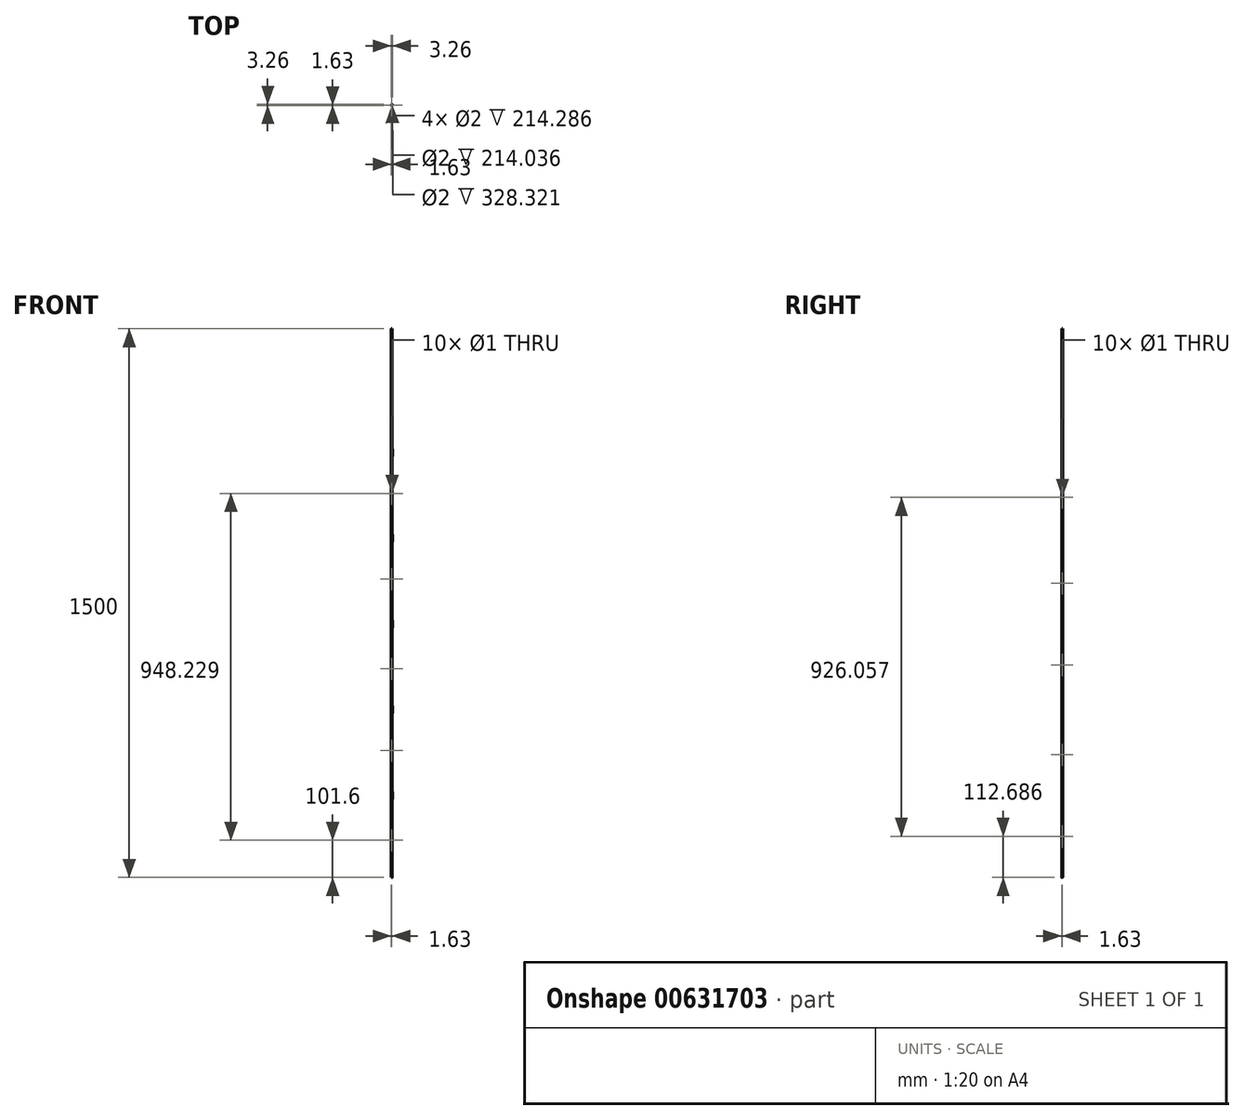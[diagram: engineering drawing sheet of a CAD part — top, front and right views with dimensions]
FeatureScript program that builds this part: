
annotation { "Feature Type Name" : "Feature", "Feature Type Description" : "" }
export const myFeature = defineFeature(function(context is Context, id is Id, definition is map)
    precondition{}
    {
        {
            var Q0;
            Q0=qCreatedBy(makeId("Top.planeOp"),FACE);
            var sketch = newSketch(context, id + "F0", { "sketchPlane" : qUnion([Q0])});
            skCircle(sketch, "E0", {"center": v(0, 0) * mm, "radius": 1 * mm});
            skCircle(sketch, "E1", {"center": v(0, 0) * mm, "radius": 1.25 * mm});
            skSolve(sketch);
        }
        {
            var Q0;
            Q0=makeQuery(id+"F0.imprint","IMPRINT",FACE,{"disambiguationData":[TD([[makeQuery(id+"F0.imprint","IMPRINT",EDGE,{"derivedFrom":sQuery(id+"F0.wireOp",EDGE,"E0")}),-1.0]])]});
            extrude(context, id + "F1", {"entities" : qUnion([Q0]), "depth" : 1500 * mm, "offsetDistance" : 25.4 * mm});
        }
        {
            var Q0;
            Q0=qCreatedBy(makeId("Front.planeOp"),FACE);
            var sketch = newSketch(context, id + "F2", { "sketchPlane" : qUnion([Q0])});
            skLineSegment(sketch, "E2.bottom", {"start": v(0, 214.29) * mm, "end": v(1.62, 214.29) * mm});
            skLineSegment(sketch, "E2.top", {"start": v(0, 234.29) * mm, "end": v(1.62, 234.29) * mm});
            skLineSegment(sketch, "E2.left", {"start": v(0, 214.29) * mm, "end": v(0, 234.29) * mm});
            skLineSegment(sketch, "E2.right", {"start": v(1.63, 214.29) * mm, "end": v(1.63, 234.29) * mm});
            skLineSegment(sketch, "E3", {"start": v(0, -76.39) * mm, "end": v(0, 107.51) * mm});
            skLineSegment(sketch, "E4.bottom", {"start": v(0, 448.57) * mm, "end": v(1.62, 448.57) * mm});
            skLineSegment(sketch, "E4.top", {"start": v(0, 468.57) * mm, "end": v(1.62, 468.57) * mm});
            skLineSegment(sketch, "E4.left", {"start": v(0, 448.57) * mm, "end": v(0, 468.57) * mm});
            skLineSegment(sketch, "E4.right", {"start": v(1.62, 448.57) * mm, "end": v(1.62, 468.57) * mm});
            skLineSegment(sketch, "E5.bottom", {"start": v(0, 682.86) * mm, "end": v(1.62, 682.86) * mm});
            skLineSegment(sketch, "E5.top", {"start": v(0, 702.86) * mm, "end": v(1.62, 702.86) * mm});
            skLineSegment(sketch, "E5.left", {"start": v(0, 682.86) * mm, "end": v(0, 702.86) * mm});
            skLineSegment(sketch, "E5.right", {"start": v(1.62, 682.86) * mm, "end": v(1.62, 702.86) * mm});
            skLineSegment(sketch, "E6.bottom", {"start": v(0, 937.14) * mm, "end": v(1.63, 937.14) * mm});
            skLineSegment(sketch, "E6.top", {"start": v(0, 917.14) * mm, "end": v(1.63, 917.14) * mm});
            skLineSegment(sketch, "E6.left", {"start": v(0, 937.14) * mm, "end": v(0, 917.14) * mm});
            skLineSegment(sketch, "E6.right", {"start": v(1.62, 937.14) * mm, "end": v(1.62, 917.14) * mm});
            skLineSegment(sketch, "E7.bottom", {"start": v(0, 1151.43) * mm, "end": v(1.62, 1151.43) * mm});
            skLineSegment(sketch, "E7.top", {"start": v(0, 1171.43) * mm, "end": v(1.62, 1171.43) * mm});
            skLineSegment(sketch, "E7.left", {"start": v(0, 1151.43) * mm, "end": v(0, 1171.43) * mm});
            skLineSegment(sketch, "E7.right", {"start": v(1.62, 1151.43) * mm, "end": v(1.62, 1171.43) * mm});
            skSolve(sketch);
        }
        {
            var Q0;
            {var subQ0=sQuery(id+"F2.wireOp",EDGE,"E2.bottom");Q0=makeQuery(id+"F2.imprint","IMPRINT",FACE,{"disambiguationData":[TD([[makeQuery(id+"F2.imprint","IMPRINT",EDGE,{"derivedFrom":subQ0}),1.0]])]});}
            var Q1;
            Q1=sQuery(id+"F2.wireOp",EDGE,"E3");
            revolve(context, id + "F3", {"operationType" : NewBodyOperationType.ADD, "entities" : qUnion([Q0]), "axis" : qUnion([Q1]), "revolveType" : RevolveType.FULL});
        }
        {
            var Q0;
            Q0=qCreatedBy(makeId("Front.planeOp"),FACE);
            var sketch = newSketch(context, id + "F4", { "sketchPlane" : qUnion([Q0])});
            skLineSegment(sketch, "E8", {"start": v(0, -76.07) * mm, "end": v(0, 1560.8) * mm});
            skSolve(sketch);
        }
        {
            var Q0;
            Q0=makeQuery(id+"F2.imprint","IMPRINT",FACE,{"disambiguationData":[TD([[makeQuery(id+"F2.imprint","IMPRINT",EDGE,{"derivedFrom":sQuery(id+"F2.wireOp",EDGE,"E4.bottom")}),1.0]])]});
            var Q1;
            Q1=sQuery(id+"F4.wireOp",EDGE,"E8");
            revolve(context, id + "F5", {"operationType" : NewBodyOperationType.ADD, "entities" : qUnion([Q0]), "axis" : qUnion([Q1]), "revolveType" : RevolveType.FULL});
        }
        {
            var Q0;
            Q0=makeQuery(id+"F2.imprint","IMPRINT",FACE,{"disambiguationData":[TD([[makeQuery(id+"F2.imprint","IMPRINT",EDGE,{"derivedFrom":sQuery(id+"F2.wireOp",EDGE,"E5.bottom")}),1.0]])]});
            var Q1;
            Q1=sQuery(id+"F4.wireOp",EDGE,"E8");
            revolve(context, id + "F6", {"operationType" : NewBodyOperationType.ADD, "entities" : qUnion([Q0]), "axis" : qUnion([Q1]), "revolveType" : RevolveType.FULL});
        }
        {
            var Q0;
            Q0=makeQuery(id+"F2.imprint","IMPRINT",FACE,{"disambiguationData":[TD([[makeQuery(id+"F2.imprint","IMPRINT",EDGE,{"derivedFrom":sQuery(id+"F2.wireOp",EDGE,"E6.bottom")}),-1.0]])]});
            var Q1;
            Q1=sQuery(id+"F4.wireOp",EDGE,"E8");
            revolve(context, id + "F7", {"entities" : qUnion([Q0]), "axis" : qUnion([Q1]), "revolveType" : RevolveType.FULL});
        }
        {
            var Q0;
            Q0=makeQuery(id+"F2.imprint","IMPRINT",FACE,{"disambiguationData":[TD([[makeQuery(id+"F2.imprint","IMPRINT",EDGE,{"derivedFrom":sQuery(id+"F2.wireOp",EDGE,"E6.bottom")}),-1.0]])]});
            var Q1;
            Q1=sQuery(id+"F4.wireOp",EDGE,"E8");
            revolve(context, id + "F8", {"operationType" : NewBodyOperationType.ADD, "entities" : qUnion([Q0]), "axis" : qUnion([Q1]), "revolveType" : RevolveType.FULL});
        }
        {
            var Q0;
            Q0=makeQuery(id+"F2.imprint","IMPRINT",FACE,{"disambiguationData":[TD([[makeQuery(id+"F2.imprint","IMPRINT",EDGE,{"derivedFrom":sQuery(id+"F2.wireOp",EDGE,"E7.bottom")}),1.0]])]});
            var Q1;
            Q1=sQuery(id+"F4.wireOp",EDGE,"E8");
            revolve(context, id + "F9", {"operationType" : NewBodyOperationType.ADD, "entities" : qUnion([Q0]), "axis" : qUnion([Q1]), "revolveType" : RevolveType.FULL});
        }
        {
            var Q0;
            Q0=qCreatedBy(makeId("Front.planeOp"),FACE);
            var sketch = newSketch(context, id + "F10", { "sketchPlane" : qUnion([Q0])});
            skCircle(sketch, "E9", {"center": v(0, 101.6) * mm, "radius": 0.5 * mm});
            skLineSegment(sketch, "E10", {"start": v(0, 224.29) * mm, "end": v(19.28, 224.29) * mm});
            skCircle(sketch, "E11.MirrorC", {"center": v(0, 346.97) * mm, "radius": 0.5 * mm});
            skSolve(sketch);
        }
        {
            var Q0;
            Q0 = qSketchRegion(id + "F10", true);
            extrude(context, id + "F11", {"entities" : qUnion([Q0]), "operationType" : NewBodyOperationType.REMOVE, "endBound" : BoundingType.SYMMETRIC, "oppositeDirection" : true, "depth" : 25.4 * mm, "offsetDistance" : 25.4 * mm});
        }
        {
            var Q0;
            Q0=qCreatedBy(makeId("Right.planeOp"),FACE);
            var sketch = newSketch(context, id + "F12", { "sketchPlane" : qUnion([Q0])});
            skCircle(sketch, "E12", {"center": v(0, 112.69) * mm, "radius": 0.5 * mm});
            skLineSegment(sketch, "E13", {"start": v(0, 224.29) * mm, "end": v(-15.1, 224.29) * mm});
            skCircle(sketch, "E14.MirrorC", {"center": v(0, 335.89) * mm, "radius": 0.5 * mm});
            skSolve(sketch);
        }
        {
            var Q0;
            Q0 = qSketchRegion(id + "F12", true);
            extrude(context, id + "F13", {"entities" : qUnion([Q0]), "operationType" : NewBodyOperationType.REMOVE, "endBound" : BoundingType.SYMMETRIC, "depth" : 25.4 * mm, "offsetDistance" : 25.4 * mm});
        }
        {
            var Q0;
            Q0=qCreatedBy(makeId("Front.planeOp"),FACE);
            var sketch = newSketch(context, id + "F14", { "sketchPlane" : qUnion([Q0])});
            skLineSegment(sketch, "E15", {"start": v(0, 692.86) * mm, "end": v(-20.67, 692.86) * mm});
            skSolve(sketch);
        }
        {
            var Q0;
            Q0=qCreatedBy(makeId("Front.planeOp"),FACE);
            var sketch = newSketch(context, id + "F15", { "sketchPlane" : qUnion([Q0])});
            skCircle(sketch, "E16", {"center": v(0, 570.17) * mm, "radius": 0.5 * mm});
            skCircle(sketch, "E17.MirrorC", {"center": v(0, 815.54) * mm, "radius": 0.5 * mm});
            skSolve(sketch);
        }
        {
            var Q0;
            Q0 = qSketchRegion(id + "F15", true);
            extrude(context, id + "F16", {"entities" : qUnion([Q0]), "operationType" : NewBodyOperationType.REMOVE, "endBound" : BoundingType.SYMMETRIC, "oppositeDirection" : true, "depth" : 25.4 * mm, "offsetDistance" : 25.4 * mm});
        }
        {
            var Q0;
            Q0=qCreatedBy(makeId("Right.planeOp"),FACE);
            var sketch = newSketch(context, id + "F17", { "sketchPlane" : qUnion([Q0])});
            skCircle(sketch, "E18", {"center": v(0, 804.46) * mm, "radius": 0.5 * mm});
            skSolve(sketch);
        }
        {
            var Q0;
            Q0 = qSketchRegion(id + "F17", true);
            extrude(context, id + "F18", {"entities" : qUnion([Q0]), "operationType" : NewBodyOperationType.REMOVE, "endBound" : BoundingType.SYMMETRIC, "depth" : 25.4 * mm, "offsetDistance" : 25.4 * mm});
        }
        {
            var Q0;
            Q0=qCreatedBy(makeId("Right.planeOp"),FACE);
            var sketch = newSketch(context, id + "F19", { "sketchPlane" : qUnion([Q0])});
            skCircle(sketch, "E19", {"center": v(0, 581.26) * mm, "radius": 0.5 * mm});
            skSolve(sketch);
        }
        {
            var Q0;
            Q0 = qSketchRegion(id + "F19", true);
            extrude(context, id + "F20", {"entities" : qUnion([Q0]), "operationType" : NewBodyOperationType.REMOVE, "endBound" : BoundingType.SYMMETRIC, "depth" : 25.4 * mm, "offsetDistance" : 25.4 * mm});
        }
        {
            var Q0;
            Q0=qCreatedBy(makeId("Right.planeOp"),FACE);
            var sketch = newSketch(context, id + "F21", { "sketchPlane" : qUnion([Q0])});
            skCircle(sketch, "E20", {"center": v(0, 1038.74) * mm, "radius": 0.5 * mm});
            skSolve(sketch);
        }
        {
            var Q0;
            Q0 = qSketchRegion(id + "F21", true);
            extrude(context, id + "F22", {"entities" : qUnion([Q0]), "operationType" : NewBodyOperationType.REMOVE, "endBound" : BoundingType.SYMMETRIC, "depth" : 25.4 * mm, "offsetDistance" : 25.4 * mm});
        }
        {
            var Q0;
            Q0=qCreatedBy(makeId("Front.planeOp"),FACE);
            var sketch = newSketch(context, id + "F23", { "sketchPlane" : qUnion([Q0])});
            skCircle(sketch, "E21", {"center": v(0, 1049.83) * mm, "radius": 0.5 * mm});
            skSolve(sketch);
        }
        {
            var Q0;
            Q0 = qSketchRegion(id + "F23", true);
            extrude(context, id + "F24", {"entities" : qUnion([Q0]), "operationType" : NewBodyOperationType.REMOVE, "endBound" : BoundingType.SYMMETRIC, "depth" : 25.4 * mm, "offsetDistance" : 25.4 * mm});
        }
        {
            var Q0;
            Q0=qCreatedBy(makeId("Top.planeOp"),FACE);
            var sketch = newSketch(context, id + "F25", { "sketchPlane" : qUnion([Q0])});
            skCircle(sketch, "E22", {"center": v(0, 0) * mm, "radius": 1 * mm});
            skSolve(sketch);
        }
        {
            var Q0;
            Q0 = qSketchRegion(id + "F25", true);
            extrude(context, id + "F26", {"entities" : qUnion([Q0]), "operationType" : NewBodyOperationType.ADD, "depth" : 0.25 * mm, "offsetDistance" : 25.4 * mm});
        }
        {
            var Q0;
            Q0=makeQuery(id+"F1.opExtrude","CAP_FACE",FACE,{"disambiguationData":[OSD([sQuery(id+"F0.wireOp",EDGE,"E0"),sQuery(id+"F0.wireOp",EDGE,"E1")])],"isStart":false});
            var sketch = newSketch(context, id + "F27", { "sketchPlane" : qUnion([Q0])});
            skCircle(sketch, "E23", {"center": v(0, 0) * mm, "radius": 1 * mm});
            skSolve(sketch);
        }
        {
            var Q0;
            Q0 = qSketchRegion(id + "F27", true);
            extrude(context, id + "F28", {"entities" : qUnion([Q0]), "operationType" : NewBodyOperationType.ADD, "oppositeDirection" : true, "depth" : 0.25 * mm, "offsetDistance" : 25.4 * mm});
        }
    });
